# Revit family: Worksurface-Teknion-PLCW__Cantilevered_Worksurface-R2015
name_source: partatom
category: Furniture
revit_build: Autodesk Revit Architecture 2015 (Build: 20140323_1530(x64)
units: mm (PartAtom-declared; Revit-internal decimal feet)

## types (2) — shared parameters
Assembly Code = E2020200
Default Elevation = 48 "
Manufacturer = Teknion
Manufacturer Fax = 416.661.4586
Part Number = PLCW
Product Documentation Link = http://www.teknion.com
Product Page URL = http://www.teknion.com
Series = Ledger Plus
Sustainability Data = http://www.teknion.com
URL = www.teknion.com
Unit Weight URL = http://www.teknion.com
Warranty = http://www.teknion.com

## per-type parameters (varying)
| type | Description | Model | Product Line |
| Single Sided Overhang | Cantilevered Worksurface - Single Sided Overhang | PLCWS_ | Filing & Storage |
| Double Sided Overhang | Cantilevered Worksurface - Double Sided Overhang | PLCWD_ | Filing and Storage |

type visibility flags: 2 boolean params named "<type name>" — each type sets only its own to Yes (folded from table)

## geometry (parser evidence)
native form markers: Sweep x3
no freeform markers — native parametric forms only
